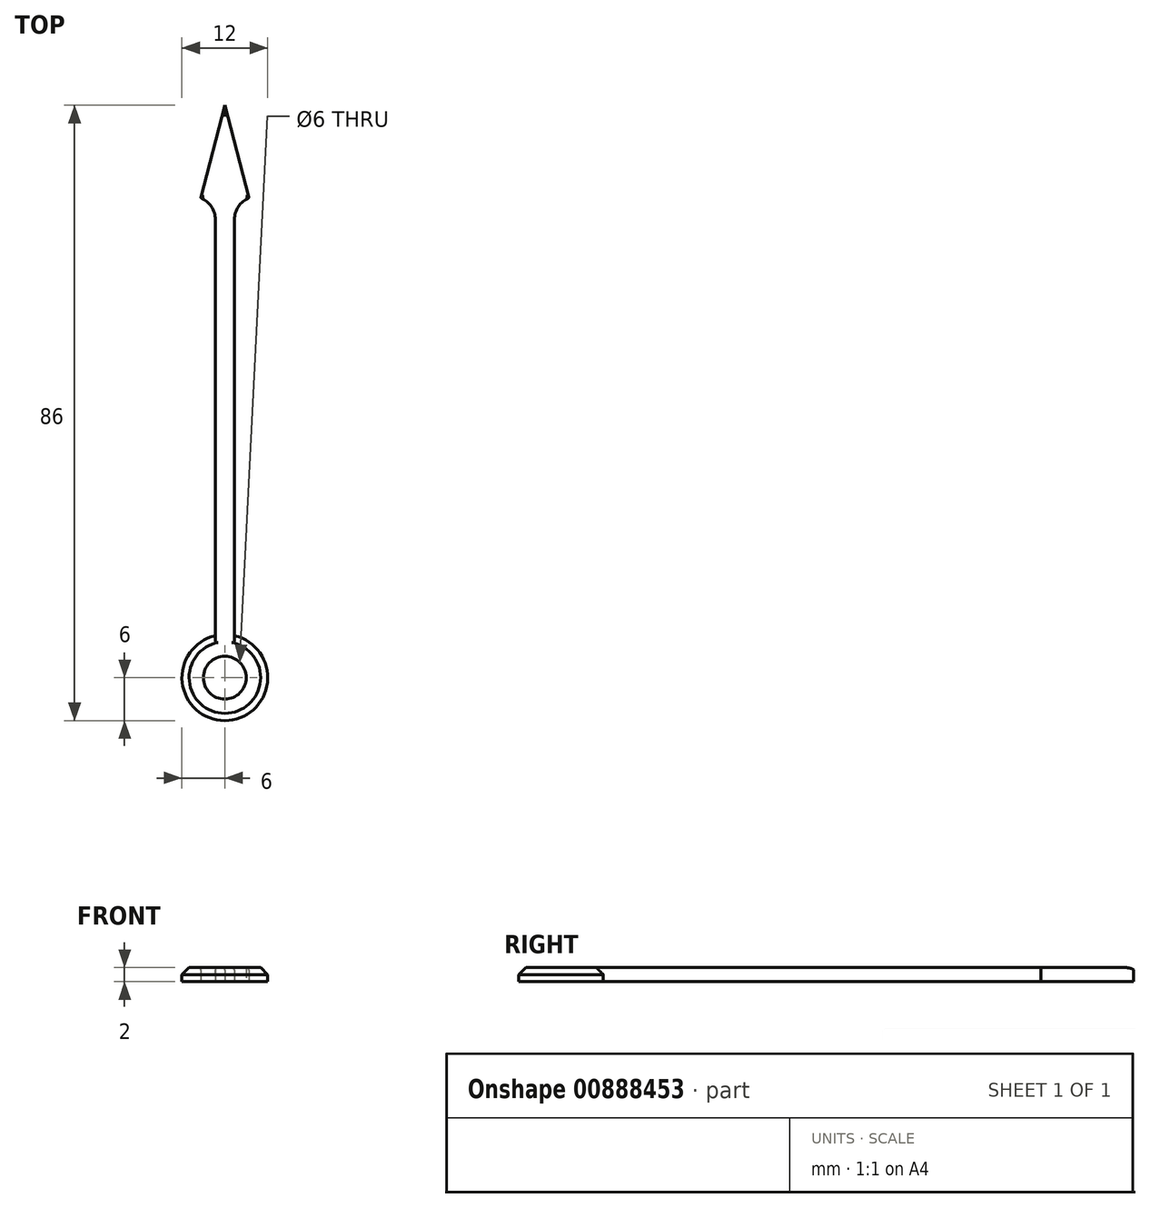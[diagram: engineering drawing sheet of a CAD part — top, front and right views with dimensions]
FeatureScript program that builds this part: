
annotation { "Feature Type Name" : "Feature", "Feature Type Description" : "" }
export const myFeature = defineFeature(function(context is Context, id is Id, definition is map)
    precondition{}
    {
        {
            var Q0;
            Q0=qCreatedBy(makeId("Top.planeOp"),FACE);
            var sketch = newSketch(context, id + "F0", { "sketchPlane" : qUnion([Q0])});
            skCircle(sketch, "E0", {"center": v(0, 0) * mm, "radius": 3 * mm});
            skArc(sketch, "E1", {"start": v(-1.34, 5.85) * mm, "mid": v(0, -6) * mm, "end": v(1.34, 5.85) * mm});
            skLineSegment(sketch, "E2", {"start": v(0, 80) * mm, "end": v(3.4, 67.05) * mm});
            skLineSegment(sketch, "E3.trimOffspring", {"start": v(3, 0.03) * mm, "end": v(3, 0) * mm});
            skLineSegment(sketch, "E4", {"start": v(1.34, 5.85) * mm, "end": v(1.34, 64) * mm});
            skArc(sketch, "E5", {"start": v(3.4, 67.05) * mm, "mid": v(1.9, 65.84) * mm, "end": v(1.34, 64) * mm});
            skArc(sketch, "E6.MirrorCS", {"start": v(-3.4, 67.05) * mm, "mid": v(-1.9, 65.84) * mm, "end": v(-1.34, 64) * mm});
            skLineSegment(sketch, "E7", {"start": v(0, 80) * mm, "end": v(-3.4, 67.05) * mm});
            skLineSegment(sketch, "E8", {"start": v(-1.34, 64) * mm, "end": v(-1.34, 5.85) * mm});
            skSolve(sketch);
        }
        {
            var Q0;
            Q0=makeQuery(id+"F0.imprint","IMPRINT",FACE,{"disambiguationData":[TD([[makeQuery(id+"F0.imprint","IMPRINT",EDGE,{"derivedFrom":sQuery(id+"F0.wireOp",EDGE,"E0")}),-1.0]])]});
            extrude(context, id + "F1", {"entities" : qUnion([Q0]), "depth" : 2 * mm, "offsetDistance" : 25 * mm});
        }
        {
            var Q0;
            Q0=makeQuery(id+"F1.opExtrude","CAP_EDGE",EDGE,{"disambiguationData":[OSD([sQuery(id+"F0.wireOp",EDGE,"E1")])],"isStart":false});
            chamfer(context, id + "F2", {"entities" : qUnion([Q0]), "width" : 1 * mm, "tangentPropagation" : true});
        }
        {
            var Q0;
            Q0=makeQuery(id+"F1.opExtrude","CAP_EDGE",EDGE,{"disambiguationData":[OSD([sQuery(id+"F0.wireOp",EDGE,"E4")])],"isStart":false});
            var Q1;
            Q1=makeQuery(id+"F1.opExtrude","CAP_EDGE",EDGE,{"disambiguationData":[OSD([sQuery(id+"F0.wireOp",EDGE,"E8")])],"isStart":false});
            var Q2;
            Q2=makeQuery(id+"F1.opExtrude","CAP_EDGE",EDGE,{"disambiguationData":[OSD([sQuery(id+"F0.wireOp",EDGE,"E2")])],"isStart":false});
            var Q3;
            Q3=makeQuery(id+"F1.opExtrude","CAP_EDGE",EDGE,{"disambiguationData":[OSD([sQuery(id+"F0.wireOp",EDGE,"E7")])],"isStart":false});
            var Q4;
            Q4=makeQuery(id+"F1.opExtrude","CAP_EDGE",EDGE,{"disambiguationData":[OSD([sQuery(id+"F0.wireOp",EDGE,"E5")])],"isStart":false});
            var Q5;
            Q5=makeQuery(id+"F1.opExtrude","CAP_EDGE",EDGE,{"disambiguationData":[OSD([sQuery(id+"F0.wireOp",EDGE,"E6.MirrorCS")])],"isStart":false});
            fillet(context, id + "F3", {"entities" : qUnion([Q0, Q1, Q2, Q3, Q4, Q5]), "radius" : 0.4 * mm, "tangentPropagation" : true, "allowEdgeOverflow" : false});
        }
    });
